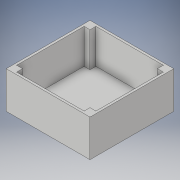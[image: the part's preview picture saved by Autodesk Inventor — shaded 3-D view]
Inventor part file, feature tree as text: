
AUTODESK INVENTOR PART (.ipt)
format: ipt  version: 2018 (Build 220112000, 112)  size: 121,856 bytes
history: native  units: in
note: dims shown in document units (in); Inventor stores cm internally (conversion verified against a paired STEP export)
features: extrude x2, sketch x2
ambient origin geometry x8: Origin, YZ Plane, XZ Plane, XY Plane, X Axis, Y Axis, Z Axis, Center Point
bodies: Solid1 (feature_tree)
feature tree (4):
  extrude  "Extrusion1"  Depth=3.621in
  extrude  "Extrusion2"  Depth=3.425in
  sketch  "Sketch1"  dims[d0=3.621in d1=3.621in]
  sketch  "Sketch2"  dims[d2=0.098in d3=0.0in d4=3.425in d5=3.425in d6=0.354in d7=0.354in d10=0.354in d11=0.354in d14=1.496in d15=0.0in]
